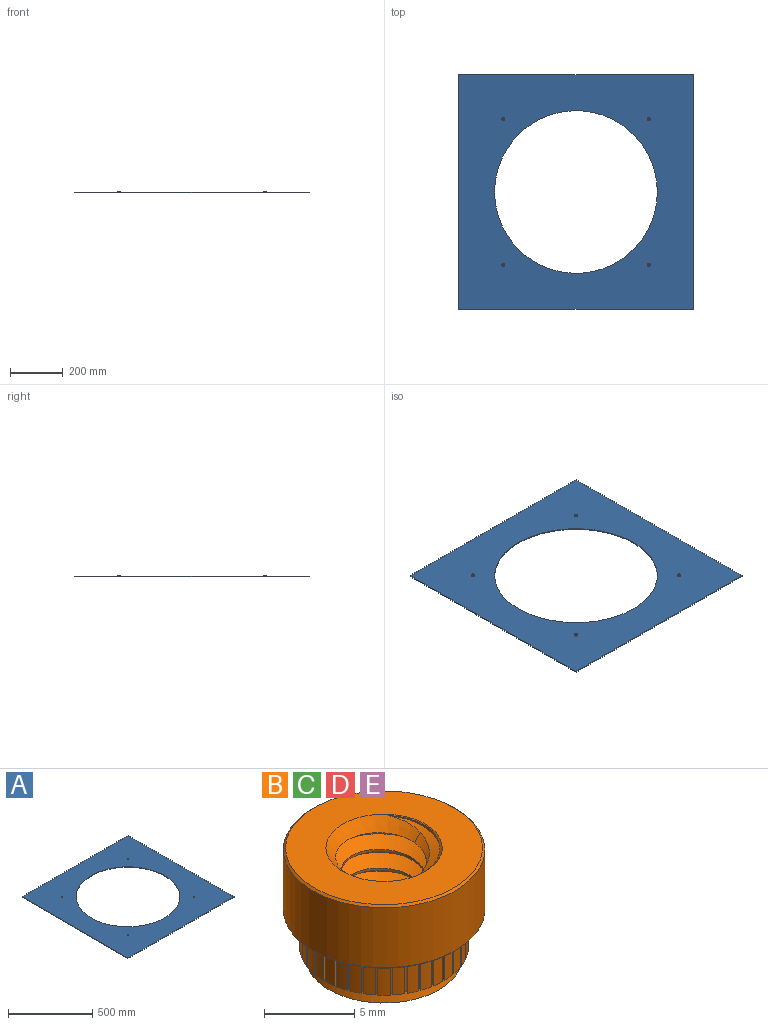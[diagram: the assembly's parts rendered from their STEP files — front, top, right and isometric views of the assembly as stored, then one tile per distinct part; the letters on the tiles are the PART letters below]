
ASSEMBLY  parts=5 mates=4
PART A: 11 faces, bbox 889x889x3.2 mm
  f0: plane 889x3.18mm, normal (0,1,0), area 2822.6mm2, adj f1,f8,f9,f10
  f1: plane 889x3.18mm, normal (-1,0,0), area 2822.6mm2, adj f0,f2,f9,f10
  f2: plane 889x3.18mm, normal (0,-1,0), area 2822.6mm2, adj f1,f8,f9,f10
  f3: cylinder r=307.98mm len=615.95mm, axis (0,0,-1), area 6143.8mm2, adj f9,f10
  f4: cylinder r=4.37mm len=8.73mm, axis (0,0,-1), area 87.1mm2, adj f9,f10
  f5: cylinder r=4.37mm len=8.73mm, axis (0,0,-1), area 87.1mm2, adj f9,f10
  f6: cylinder r=4.37mm len=8.73mm, axis (0,0,-1), area 87.1mm2, adj f9,f10
  f7: cylinder r=4.37mm len=8.73mm, axis (0,0,-1), area 87.1mm2, adj f9,f10
  f8: plane 889x3.18mm, normal (1,0,0), area 2822.6mm2, adj f0,f2,f9,f10
  f9: plane 889x889mm, normal (0,0,1), area 492105.8mm2, adj f0,f1,f2,f3,f4,f5,f6,f7
  f10: plane 889x889mm, normal (0,0,-1), area 492105.8mm2, adj f0,f1,f2,f3,f4,f5,f6,f7
PART B: 159 faces, bbox 11.2x11.2x8.5 mm
  f0: bspline ~8.1x7.33mm, area 86.2mm2, adj f1,f3,f156,f157,f158
  f1: cylinder r=2.35mm len=5.74mm, axis (0,0,1), area 10.2mm2, adj f0,f2,f157,f158
  f2: bspline ~8.1x7.33mm, area 86.2mm2, adj f1,f3,f156,f157,f158
  f3: cylinder r=3.17mm len=7.39mm, axis (0,0,1), area 14.9mm2, adj f0,f2,f156,f158
  f4: cylinder r=4.69mm len=2.38mm, axis (0,0,1), area 1.6mm2, adj f142,f146,f148,f151
  f5: cylinder r=4.69mm len=2.38mm, axis (0,0,1), area 1.6mm2, adj f139,f143,f148,f151
  f6: cylinder r=4.69mm len=2.38mm, axis (0,0,1), area 1.6mm2, adj f136,f140,f148,f151
  f7: cylinder r=4.69mm len=2.38mm, axis (0,0,1), area 1.6mm2, adj f133,f137,f148,f151
  f8: cylinder r=4.69mm len=2.38mm, axis (0,0,1), area 1.6mm2, adj f130,f134,f148,f151
  f9: cylinder r=4.69mm len=2.38mm, axis (0,0,1), area 1.6mm2, adj f127,f131,f148,f151
  f10: cylinder r=4.69mm len=2.38mm, axis (0,0,1), area 1.6mm2, adj f124,f128,f148,f151
  f11: cylinder r=4.69mm len=2.38mm, axis (0,0,1), area 1.6mm2, adj f121,f125,f148,f151
  f12: cylinder r=4.69mm len=2.38mm, axis (0,0,1), area 1.6mm2, adj f118,f122,f148,f151
  f13: cylinder r=4.69mm len=2.38mm, axis (0,0,1), area 1.6mm2, adj f115,f119,f148,f151
  f14: cylinder r=4.69mm len=2.38mm, axis (0,0,1), area 1.6mm2, adj f112,f116,f148,f151
  f15: cylinder r=4.69mm len=2.38mm, axis (0,0,1), area 1.6mm2, adj f109,f113,f148,f151
  f16: cylinder r=4.69mm len=2.38mm, axis (0,0,1), area 1.6mm2, adj f106,f110,f148,f151
  f17: cylinder r=4.69mm len=2.38mm, axis (0,0,1), area 1.6mm2, adj f103,f107,f148,f151
  f18: cylinder r=4.69mm len=2.38mm, axis (0,0,1), area 1.6mm2, adj f100,f104,f148,f151
  f19: cylinder r=4.69mm len=2.38mm, axis (0,0,1), area 1.6mm2, adj f97,f101,f148,f151
  f20: cylinder r=4.69mm len=2.38mm, axis (0,0,1), area 1.6mm2, adj f94,f98,f148,f151
  f21: cylinder r=4.69mm len=2.38mm, axis (0,0,1), area 1.6mm2, adj f91,f95,f148,f151
  f22: cylinder r=4.69mm len=2.38mm, axis (0,0,1), area 1.6mm2, adj f88,f92,f148,f151
  f23: cylinder r=4.69mm len=2.38mm, axis (0,0,1), area 1.6mm2, adj f85,f89,f148,f151
  f24: cylinder r=4.69mm len=2.38mm, axis (0,0,1), area 1.6mm2, adj f82,f86,f148,f151
  f25: cylinder r=4.69mm len=2.38mm, axis (0,0,1), area 1.6mm2, adj f79,f83,f148,f151
  f26: cylinder r=4.69mm len=2.38mm, axis (0,0,1), area 1.6mm2, adj f76,f80,f148,f151
  f27: cylinder r=4.69mm len=2.38mm, axis (0,0,1), area 1.6mm2, adj f73,f77,f148,f151
  f28: cylinder r=4.69mm len=2.38mm, axis (0,0,1), area 1.6mm2, adj f70,f74,f148,f151
  f29: cylinder r=4.69mm len=2.38mm, axis (0,0,1), area 1.6mm2, adj f67,f71,f148,f151
  f30: cylinder r=4.69mm len=2.38mm, axis (0,0,1), area 1.6mm2, adj f64,f68,f148,f151
  f31: cylinder r=4.69mm len=2.38mm, axis (0,0,1), area 1.6mm2, adj f61,f65,f148,f151
  f32: cylinder r=4.69mm len=2.38mm, axis (0,0,1), area 1.6mm2, adj f58,f62,f148,f151
  f33: cylinder r=4.69mm len=2.38mm, axis (0,0,1), area 1.6mm2, adj f55,f59,f148,f151
  f34: cylinder r=4.69mm len=2.38mm, axis (0,0,1), area 1.6mm2, adj f52,f56,f148,f151
  f35: cylinder r=4.69mm len=2.38mm, axis (0,0,1), area 1.6mm2, adj f49,f53,f148,f151
  f36: cylinder r=4.69mm len=2.38mm, axis (0,0,1), area 1.6mm2, adj f46,f50,f148,f151
  f37: cylinder r=4.69mm len=2.38mm, axis (0,0,1), area 1.6mm2, adj f43,f47,f148,f151
  f38: cylinder r=4.69mm len=2.38mm, axis (0,0,1), area 1.6mm2, adj f40,f44,f148,f151
  f39: cylinder r=4.69mm len=2.38mm, axis (0,0,1), area 1.6mm2, adj f41,f145,f148,f151
  f40: plane 2.38x0.19mm, normal (1,0,0), area 0.5mm2, adj f38,f42,f148,f151
  f41: plane 2.38x0.19mm, normal (-1,0,0), area 0.5mm2, adj f39,f42,f148,f151
  f42: plane 2.38x0.13mm, normal (0,1,0), area 0.3mm2, adj f40,f41,f148,f151
  f43: plane 2.38x0.19mm, normal (0.98,0.17,0), area 0.5mm2, adj f37,f45,f148,f151
  f44: plane 2.38x0.19mm, normal (-0.98,-0.17,0), area 0.5mm2, adj f38,f45,f148,f151
  f45: plane 2.38x0.13mm, normal (-0.17,0.98,0), area 0.3mm2, adj f43,f44,f148,f151
  f46: plane 2.38x0.18mm, normal (0.94,0.34,0), area 0.5mm2, adj f36,f48,f148,f151
  f47: plane 2.38x0.18mm, normal (-0.94,-0.34,0), area 0.5mm2, adj f37,f48,f148,f151
  f48: plane 2.38x0.12mm, normal (-0.34,0.94,0), area 0.3mm2, adj f46,f47,f148,f151
  f49: plane 2.38x0.16mm, normal (0.87,0.5,0), area 0.5mm2, adj f35,f51,f148,f151
  f50: plane 2.38x0.16mm, normal (-0.87,-0.5,0), area 0.5mm2, adj f36,f51,f148,f151
  f51: plane 2.38x0.11mm, normal (-0.5,0.87,0), area 0.3mm2, adj f49,f50,f148,f151
  f52: plane 2.38x0.15mm, normal (0.77,0.64,0), area 0.5mm2, adj f34,f54,f148,f151
  f53: plane 2.38x0.15mm, normal (-0.77,-0.64,0), area 0.5mm2, adj f35,f54,f148,f151
  f54: plane 2.38x0.1mm, normal (-0.64,0.77,0), area 0.3mm2, adj f52,f53,f148,f151
  f55: plane 2.38x0.15mm, normal (0.64,0.77,0), area 0.5mm2, adj f33,f57,f148,f151
  f56: plane 2.38x0.15mm, normal (-0.64,-0.77,0), area 0.5mm2, adj f34,f57,f148,f151
  f57: plane 2.38x0.1mm, normal (-0.77,0.64,0), area 0.3mm2, adj f55,f56,f148,f151
  f58: plane 2.38x0.16mm, normal (0.5,0.87,0), area 0.5mm2, adj f32,f60,f148,f151
  f59: plane 2.38x0.16mm, normal (-0.5,-0.87,0), area 0.5mm2, adj f33,f60,f148,f151
  f60: plane 2.38x0.11mm, normal (-0.87,0.5,0), area 0.3mm2, adj f58,f59,f148,f151
  f61: plane 2.38x0.18mm, normal (0.34,0.94,0), area 0.5mm2, adj f31,f63,f148,f151
  f62: plane 2.38x0.18mm, normal (-0.34,-0.94,0), area 0.5mm2, adj f32,f63,f148,f151
  f63: plane 2.38x0.12mm, normal (-0.94,0.34,0), area 0.3mm2, adj f61,f62,f148,f151
  f64: plane 2.38x0.19mm, normal (0.17,0.98,0), area 0.5mm2, adj f30,f66,f148,f151
  f65: plane 2.38x0.19mm, normal (-0.17,-0.98,0), area 0.5mm2, adj f31,f66,f148,f151
  f66: plane 2.38x0.13mm, normal (-0.98,0.17,0), area 0.3mm2, adj f64,f65,f148,f151
  f67: plane 2.38x0.19mm, normal (0,1,0), area 0.5mm2, adj f29,f69,f148,f151
  f68: plane 2.38x0.19mm, normal (0,-1,0), area 0.5mm2, adj f30,f69,f148,f151
  f69: plane 2.38x0.13mm, normal (-1,0,0), area 0.3mm2, adj f67,f68,f148,f151
  f70: plane 2.38x0.19mm, normal (-0.17,0.98,0), area 0.5mm2, adj f28,f72,f148,f151
  f71: plane 2.38x0.19mm, normal (0.17,-0.98,0), area 0.5mm2, adj f29,f72,f148,f151
  f72: plane 2.38x0.13mm, normal (-0.98,-0.17,0), area 0.3mm2, adj f70,f71,f148,f151
  f73: plane 2.38x0.18mm, normal (-0.34,0.94,0), area 0.5mm2, adj f27,f75,f148,f151
  f74: plane 2.38x0.18mm, normal (0.34,-0.94,0), area 0.5mm2, adj f28,f75,f148,f151
  f75: plane 2.38x0.12mm, normal (-0.94,-0.34,0), area 0.3mm2, adj f73,f74,f148,f151
  f76: plane 2.38x0.16mm, normal (-0.5,0.87,0), area 0.5mm2, adj f26,f78,f148,f151
  f77: plane 2.38x0.16mm, normal (0.5,-0.87,0), area 0.5mm2, adj f27,f78,f148,f151
  f78: plane 2.38x0.11mm, normal (-0.87,-0.5,0), area 0.3mm2, adj f76,f77,f148,f151
  f79: plane 2.38x0.15mm, normal (-0.64,0.77,0), area 0.5mm2, adj f25,f81,f148,f151
  f80: plane 2.38x0.15mm, normal (0.64,-0.77,0), area 0.5mm2, adj f26,f81,f148,f151
  f81: plane 2.38x0.1mm, normal (-0.77,-0.64,0), area 0.3mm2, adj f79,f80,f148,f151
  f82: plane 2.38x0.15mm, normal (-0.77,0.64,0), area 0.5mm2, adj f24,f84,f148,f151
  f83: plane 2.38x0.15mm, normal (0.77,-0.64,0), area 0.5mm2, adj f25,f84,f148,f151
  f84: plane 2.38x0.1mm, normal (-0.64,-0.77,0), area 0.3mm2, adj f82,f83,f148,f151
  f85: plane 2.38x0.16mm, normal (-0.87,0.5,0), area 0.5mm2, adj f23,f87,f148,f151
  f86: plane 2.38x0.16mm, normal (0.87,-0.5,0), area 0.5mm2, adj f24,f87,f148,f151
  f87: plane 2.38x0.11mm, normal (-0.5,-0.87,0), area 0.3mm2, adj f85,f86,f148,f151
  f88: plane 2.38x0.18mm, normal (-0.94,0.34,0), area 0.5mm2, adj f22,f90,f148,f151
  f89: plane 2.38x0.18mm, normal (0.94,-0.34,0), area 0.5mm2, adj f23,f90,f148,f151
  f90: plane 2.38x0.12mm, normal (-0.34,-0.94,0), area 0.3mm2, adj f88,f89,f148,f151
  f91: plane 2.38x0.19mm, normal (-0.98,0.17,0), area 0.5mm2, adj f21,f93,f148,f151
  f92: plane 2.38x0.19mm, normal (0.98,-0.17,0), area 0.5mm2, adj f22,f93,f148,f151
  f93: plane 2.38x0.13mm, normal (-0.17,-0.98,0), area 0.3mm2, adj f91,f92,f148,f151
  f94: plane 2.38x0.19mm, normal (-1,0,0), area 0.5mm2, adj f20,f96,f148,f151
  f95: plane 2.38x0.19mm, normal (1,0,0), area 0.5mm2, adj f21,f96,f148,f151
  f96: plane 2.38x0.13mm, normal (0,-1,0), area 0.3mm2, adj f94,f95,f148,f151
  f97: plane 2.38x0.19mm, normal (-0.98,-0.17,0), area 0.5mm2, adj f19,f99,f148,f151
  f98: plane 2.38x0.19mm, normal (0.98,0.17,0), area 0.5mm2, adj f20,f99,f148,f151
  f99: plane 2.38x0.13mm, normal (0.17,-0.98,0), area 0.3mm2, adj f97,f98,f148,f151
  f100: plane 2.38x0.18mm, normal (-0.94,-0.34,0), area 0.5mm2, adj f18,f102,f148,f151
  f101: plane 2.38x0.18mm, normal (0.94,0.34,0), area 0.5mm2, adj f19,f102,f148,f151
  f102: plane 2.38x0.12mm, normal (0.34,-0.94,0), area 0.3mm2, adj f100,f101,f148,f151
  f103: plane 2.38x0.16mm, normal (-0.87,-0.5,0), area 0.5mm2, adj f17,f105,f148,f151
  f104: plane 2.38x0.16mm, normal (0.87,0.5,0), area 0.5mm2, adj f18,f105,f148,f151
  f105: plane 2.38x0.11mm, normal (0.5,-0.87,0), area 0.3mm2, adj f103,f104,f148,f151
  f106: plane 2.38x0.15mm, normal (-0.77,-0.64,0), area 0.5mm2, adj f16,f108,f148,f151
  f107: plane 2.38x0.15mm, normal (0.77,0.64,0), area 0.5mm2, adj f17,f108,f148,f151
  f108: plane 2.38x0.1mm, normal (0.64,-0.77,0), area 0.3mm2, adj f106,f107,f148,f151
  f109: plane 2.38x0.15mm, normal (-0.64,-0.77,0), area 0.5mm2, adj f15,f111,f148,f151
  f110: plane 2.38x0.15mm, normal (0.64,0.77,0), area 0.5mm2, adj f16,f111,f148,f151
  f111: plane 2.38x0.1mm, normal (0.77,-0.64,0), area 0.3mm2, adj f109,f110,f148,f151
  f112: plane 2.38x0.16mm, normal (-0.5,-0.87,0), area 0.5mm2, adj f14,f114,f148,f151
  f113: plane 2.38x0.16mm, normal (0.5,0.87,0), area 0.5mm2, adj f15,f114,f148,f151
  f114: plane 2.38x0.11mm, normal (0.87,-0.5,0), area 0.3mm2, adj f112,f113,f148,f151
  f115: plane 2.38x0.18mm, normal (-0.34,-0.94,0), area 0.5mm2, adj f13,f117,f148,f151
  f116: plane 2.38x0.18mm, normal (0.34,0.94,0), area 0.5mm2, adj f14,f117,f148,f151
  f117: plane 2.38x0.12mm, normal (0.94,-0.34,0), area 0.3mm2, adj f115,f116,f148,f151
  f118: plane 2.38x0.19mm, normal (-0.17,-0.98,0), area 0.5mm2, adj f12,f120,f148,f151
  f119: plane 2.38x0.19mm, normal (0.17,0.98,0), area 0.5mm2, adj f13,f120,f148,f151
  f120: plane 2.38x0.13mm, normal (0.98,-0.17,0), area 0.3mm2, adj f118,f119,f148,f151
  f121: plane 2.38x0.19mm, normal (0,-1,0), area 0.5mm2, adj f11,f123,f148,f151
  f122: plane 2.38x0.19mm, normal (0,1,0), area 0.5mm2, adj f12,f123,f148,f151
  f123: plane 2.38x0.13mm, normal (1,0,0), area 0.3mm2, adj f121,f122,f148,f151
  f124: plane 2.38x0.19mm, normal (0.17,-0.98,0), area 0.5mm2, adj f10,f126,f148,f151
  f125: plane 2.38x0.19mm, normal (-0.17,0.98,0), area 0.5mm2, adj f11,f126,f148,f151
  f126: plane 2.38x0.13mm, normal (0.98,0.17,0), area 0.3mm2, adj f124,f125,f148,f151
  f127: plane 2.38x0.18mm, normal (0.34,-0.94,0), area 0.5mm2, adj f9,f129,f148,f151
  f128: plane 2.38x0.18mm, normal (-0.34,0.94,0), area 0.5mm2, adj f10,f129,f148,f151
  f129: plane 2.38x0.12mm, normal (0.94,0.34,0), area 0.3mm2, adj f127,f128,f148,f151
  f130: plane 2.38x0.16mm, normal (0.5,-0.87,0), area 0.5mm2, adj f8,f132,f148,f151
  f131: plane 2.38x0.16mm, normal (-0.5,0.87,0), area 0.5mm2, adj f9,f132,f148,f151
  f132: plane 2.38x0.11mm, normal (0.87,0.5,0), area 0.3mm2, adj f130,f131,f148,f151
  f133: plane 2.38x0.15mm, normal (0.64,-0.77,0), area 0.5mm2, adj f7,f135,f148,f151
  f134: plane 2.38x0.15mm, normal (-0.64,0.77,0), area 0.5mm2, adj f8,f135,f148,f151
  f135: plane 2.38x0.1mm, normal (0.77,0.64,0), area 0.3mm2, adj f133,f134,f148,f151
  f136: plane 2.38x0.15mm, normal (0.77,-0.64,0), area 0.5mm2, adj f6,f138,f148,f151
  f137: plane 2.38x0.15mm, normal (-0.77,0.64,0), area 0.5mm2, adj f7,f138,f148,f151
  f138: plane 2.38x0.1mm, normal (0.64,0.77,0), area 0.3mm2, adj f136,f137,f148,f151
  f139: plane 2.38x0.16mm, normal (0.87,-0.5,0), area 0.5mm2, adj f5,f141,f148,f151
  f140: plane 2.38x0.16mm, normal (-0.87,0.5,0), area 0.5mm2, adj f6,f141,f148,f151
  f141: plane 2.38x0.11mm, normal (0.5,0.87,0), area 0.3mm2, adj f139,f140,f148,f151
  f142: plane 2.38x0.18mm, normal (0.94,-0.34,0), area 0.5mm2, adj f4,f144,f148,f151
  f143: plane 2.38x0.18mm, normal (-0.94,0.34,0), area 0.5mm2, adj f5,f144,f148,f151
  f144: plane 2.38x0.12mm, normal (0.34,0.94,0), area 0.3mm2, adj f142,f143,f148,f151
  f145: plane 2.38x0.19mm, normal (0.98,-0.17,0), area 0.5mm2, adj f39,f147,f148,f151
  f146: plane 2.38x0.19mm, normal (-0.98,0.17,0), area 0.5mm2, adj f4,f147,f148,f151
  f147: plane 2.38x0.13mm, normal (0.17,0.98,0), area 0.3mm2, adj f145,f146,f148,f151
  f148: plane 10.92x10.92mm, normal (0,0,-1), area 25.6mm2, adj f4,f5,f6,f7,f8,f9,f10,f11
  f149: cylinder r=5.59mm len=11.18mm, axis (0,0,1), area 142.7mm2, adj f154,f155
  f150: plane 10.92x10.92mm, normal (0,0,1), area 61mm2, adj f154,f156
  f151: plane 9.37x9.37mm, normal (0,0,-1), area 17.1mm2, adj f4,f5,f6,f7,f8,f9,f10,f11
  f152: cone r=4.32mm half-angle=20deg, axis (0,0,-1), area 22.2mm2, adj f151,f153
  f153: plane 8.64x8.64mm, normal (0,0,-1), area 25.9mm2, adj f152,f158
  f154: cone r=5.46mm half-angle=45deg, axis (0,0,-1), area 6.2mm2, adj f149,f150
  f155: cone r=5.59mm half-angle=45deg, axis (0,0,1), area 6.2mm2, adj f148,f149
  f156: cone r=3.23mm half-angle=45deg, axis (0,0,1), area 11mm2, adj f0,f2,f3,f150,f157
  f157: cone r=3.23mm half-angle=45deg, axis (0,0,1), area 0.9mm2, adj f0,f1,f2,f156
  f158: cone r=3.23mm half-angle=45deg, axis (0,0,-1), area 11.9mm2, adj f0,f1,f2,f3,f153
PART C: same geometry as B
PART D: same geometry as B
PART E: same geometry as B
PLACE A t=(-1698.64,150.43,-196.79)mm
PLACE B t=(296.14,471.17,-189.3)mm
PLACE C t=(296.14,-81.28,-189.3)mm
PLACE D t=(848.59,471.17,-189.3)mm
PLACE E t=(848.59,-81.28,-189.3)mm
MATE fastened B.f1 <-> A.f5  axis (0,0,-1) through (296.14,471.17,-193.62)mm
MATE fastened D.f1 <-> A.f6  axis (0,0,-1) through (848.59,471.17,-193.62)mm
MATE fastened E.f1 <-> A.f7  axis (0,0,-1) through (848.59,-81.28,-193.62)mm
MATE fastened C.f1 <-> A.f4  axis (0,0,-1) through (296.14,-81.28,-193.62)mm
